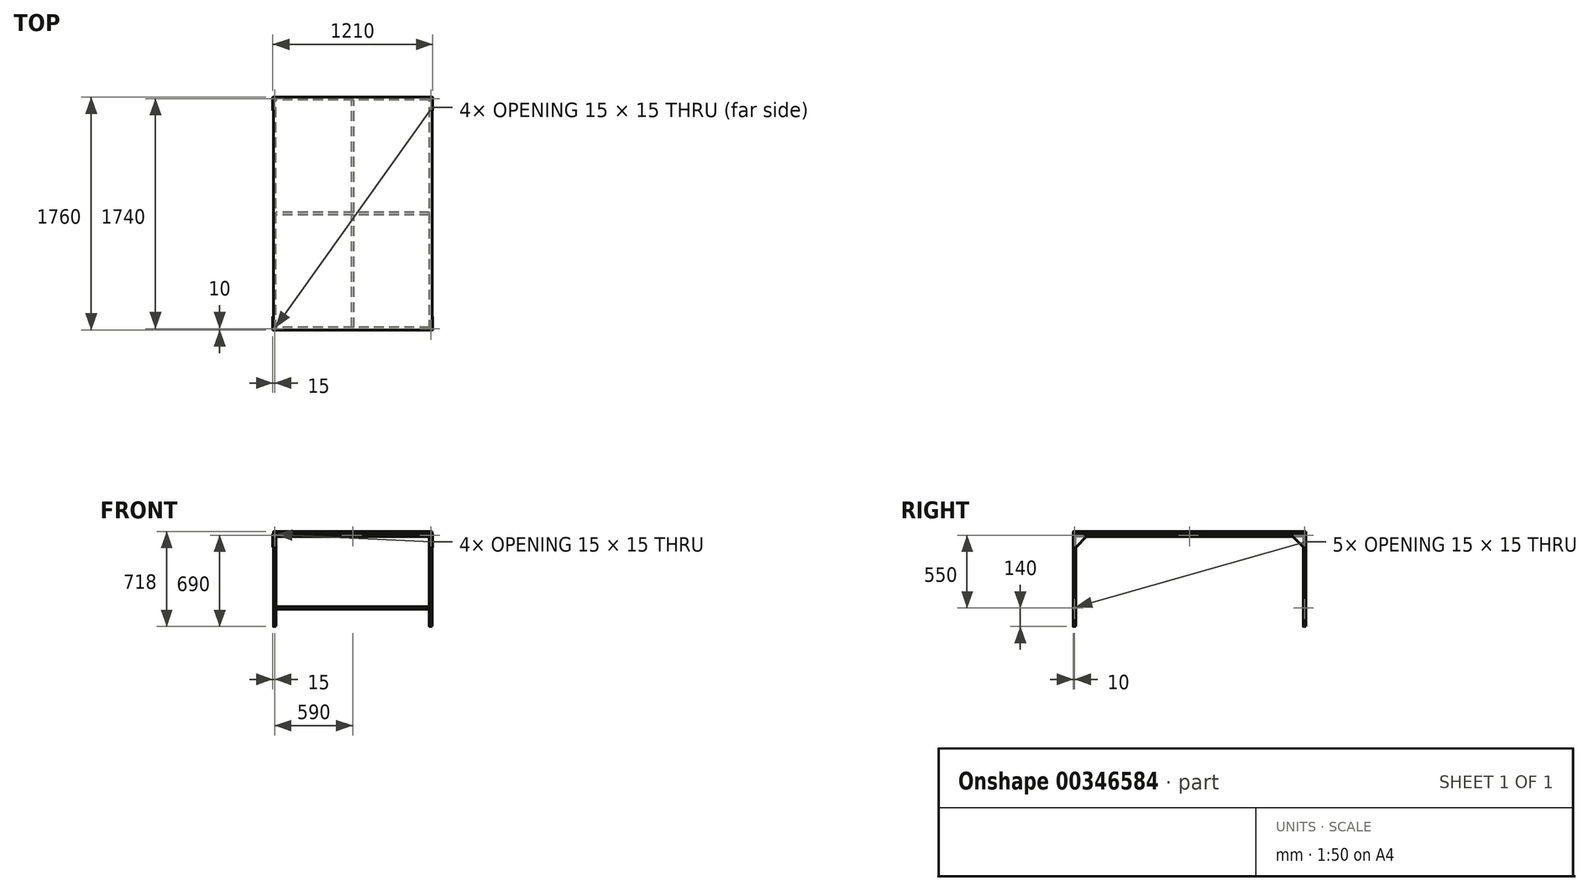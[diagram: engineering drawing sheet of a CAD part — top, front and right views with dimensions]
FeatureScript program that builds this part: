
annotation { "Feature Type Name" : "Feature", "Feature Type Description" : "" }
export const myFeature = defineFeature(function(context is Context, id is Id, definition is map)
    precondition{}
    {
        {
            var Q0;
            Q0=qCreatedBy(makeId("Front.planeOp"),FACE);
            var sketch = newSketch(context, id + "F0", { "sketchPlane" : qUnion([Q0])});
            skLineSegment(sketch, "E0.bottom", {"start": v(585, 20) * mm, "end": v(595, 20) * mm});
            skLineSegment(sketch, "E0.top", {"start": v(585, 0) * mm, "end": v(595, 0) * mm});
            skLineSegment(sketch, "E0.left", {"start": v(580, 15) * mm, "end": v(580, 5) * mm});
            skLineSegment(sketch, "E0.right", {"start": v(600, 15) * mm, "end": v(600, 5) * mm});
            skPoint(sketch, "E1.visualSharp", {"position": v(580, 20) * mm});
            skArc(sketch, "E1.filletArc", {"start": v(585, 20) * mm, "mid": v(581.46, 18.54) * mm, "end": v(580, 15) * mm});
            skPoint(sketch, "E2.visualSharp", {"position": v(600, 20) * mm});
            skArc(sketch, "E2.filletArc", {"start": v(600, 15) * mm, "mid": v(598.54, 18.54) * mm, "end": v(595, 20) * mm});
            skPoint(sketch, "E3.visualSharp", {"position": v(600, 0) * mm});
            skArc(sketch, "E3.filletArc", {"start": v(595, 0) * mm, "mid": v(598.54, 1.46) * mm, "end": v(600, 5) * mm});
            skPoint(sketch, "E4.visualSharp", {"position": v(580, 0) * mm});
            skArc(sketch, "E4.filletArc", {"start": v(580, 5) * mm, "mid": v(581.46, 1.46) * mm, "end": v(585, 0) * mm});
            skArc(sketch, "E5.0", {"start": v(585, 17.5) * mm, "mid": v(583.23, 16.77) * mm, "end": v(582.5, 15) * mm});
            skLineSegment(sketch, "E5.1", {"start": v(582.5, 15) * mm, "end": v(582.5, 5) * mm});
            skLineSegment(sketch, "E5.2", {"start": v(585, 17.5) * mm, "end": v(595, 17.5) * mm});
            skArc(sketch, "E5.3", {"start": v(582.5, 5) * mm, "mid": v(583.23, 3.23) * mm, "end": v(585, 2.5) * mm});
            skArc(sketch, "E5.4", {"start": v(597.5, 15) * mm, "mid": v(596.77, 16.77) * mm, "end": v(595, 17.5) * mm});
            skLineSegment(sketch, "E5.5", {"start": v(597.5, 15) * mm, "end": v(597.5, 5) * mm});
            skArc(sketch, "E5.6", {"start": v(595, 2.5) * mm, "mid": v(596.77, 3.23) * mm, "end": v(597.5, 5) * mm});
            skLineSegment(sketch, "E5.7", {"start": v(585, 2.5) * mm, "end": v(595, 2.5) * mm});
            skSolve(sketch);
        }
        {
            var Q0;
            Q0 = qSketchRegion(id + "F0", true);
            extrude(context, id + "F1", {"entities" : qUnion([Q0]), "endBound" : BoundingType.SYMMETRIC, "depth" : 1760 * mm});
        }
        {
            var Q0;
            Q0=makeQuery(id+"F1.opExtrude","SWEPT_BODY",BODY,{"disambiguationData":[OSD([sQuery(id+"F0.wireOp",EDGE,"E0.bottom"),sQuery(id+"F0.wireOp",EDGE,"E0.top"),sQuery(id+"F0.wireOp",EDGE,"E0.left"),sQuery(id+"F0.wireOp",EDGE,"E0.right"),sQuery(id+"F0.wireOp",EDGE,"E1.filletArc"),sQuery(id+"F0.wireOp",EDGE,"E2.filletArc"),sQuery(id+"F0.wireOp",EDGE,"E3.filletArc"),sQuery(id+"F0.wireOp",EDGE,"E4.filletArc"),sQuery(id+"F0.wireOp",EDGE,"E5.0"),sQuery(id+"F0.wireOp",EDGE,"E5.1"),sQuery(id+"F0.wireOp",EDGE,"E5.2"),sQuery(id+"F0.wireOp",EDGE,"E5.3"),sQuery(id+"F0.wireOp",EDGE,"E5.4"),sQuery(id+"F0.wireOp",EDGE,"E5.5"),sQuery(id+"F0.wireOp",EDGE,"E5.6"),sQuery(id+"F0.wireOp",EDGE,"E5.7")])]});
            transform(context, id + "F2", {"entities" : qUnion([Q0]), "transformType" : TransformType.TRANSLATION_3D, "dx" : -1180 * mm, "dy" : 0 * mm, "dz" : 0 * mm, "makeCopy" : true});
        }
        {
            var Q0;
            Q0=makeQuery(id+"F2.opPattern","COPY",FACE,{"derivedFrom":makeQuery(id+"F1.opExtrude","SWEPT_FACE",FACE,{"disambiguationData":[OSD([sQuery(id+"F0.wireOp",EDGE,"E0.right")])]}),"instanceName":"1"});
            var sketch = newSketch(context, id + "F3", { "sketchPlane" : qUnion([Q0])});
            skLineSegment(sketch, "E6.bottom", {"start": v(-875, 20) * mm, "end": v(-865, 20) * mm});
            skLineSegment(sketch, "E6.top", {"start": v(-875, 0) * mm, "end": v(-865, 0) * mm});
            skLineSegment(sketch, "E6.left", {"start": v(-880, 15) * mm, "end": v(-880, 5) * mm});
            skLineSegment(sketch, "E6.right", {"start": v(-860, 15) * mm, "end": v(-860, 5) * mm});
            skPoint(sketch, "E7.visualSharp", {"position": v(-880, 0) * mm});
            skArc(sketch, "E7.filletArc", {"start": v(-880, 5) * mm, "mid": v(-878.54, 1.46) * mm, "end": v(-875, 0) * mm});
            skPoint(sketch, "E8.visualSharp", {"position": v(-880, 20) * mm});
            skArc(sketch, "E8.filletArc", {"start": v(-875, 20) * mm, "mid": v(-878.54, 18.54) * mm, "end": v(-880, 15) * mm});
            skPoint(sketch, "E9.visualSharp", {"position": v(-860, 20) * mm});
            skArc(sketch, "E9.filletArc", {"start": v(-860, 15) * mm, "mid": v(-861.46, 18.54) * mm, "end": v(-865, 20) * mm});
            skPoint(sketch, "E10.visualSharp", {"position": v(-860, 0) * mm});
            skArc(sketch, "E10.filletArc", {"start": v(-865, 0) * mm, "mid": v(-861.46, 1.46) * mm, "end": v(-860, 5) * mm});
            skLineSegment(sketch, "E11.0", {"start": v(-877.5, 15) * mm, "end": v(-877.5, 5) * mm});
            skArc(sketch, "E11.1", {"start": v(-875, 17.5) * mm, "mid": v(-876.77, 16.77) * mm, "end": v(-877.5, 15) * mm});
            skArc(sketch, "E11.2", {"start": v(-877.5, 5) * mm, "mid": v(-876.77, 3.23) * mm, "end": v(-875, 2.5) * mm});
            skLineSegment(sketch, "E11.3", {"start": v(-875, 17.5) * mm, "end": v(-865, 17.5) * mm});
            skLineSegment(sketch, "E11.4", {"start": v(-875, 2.5) * mm, "end": v(-865, 2.5) * mm});
            skArc(sketch, "E11.5", {"start": v(-865, 2.5) * mm, "mid": v(-863.23, 3.23) * mm, "end": v(-862.5, 5) * mm});
            skLineSegment(sketch, "E11.6", {"start": v(-862.5, 15) * mm, "end": v(-862.5, 5) * mm});
            skArc(sketch, "E11.7", {"start": v(-862.5, 15) * mm, "mid": v(-863.23, 16.77) * mm, "end": v(-865, 17.5) * mm});
            skSolve(sketch);
        }
        {
            var Q0;
            Q0 = qSketchRegion(id + "F3", true);
            extrude(context, id + "F4", {"entities" : qUnion([Q0]), "depth" : 1160 * mm});
        }
        {
            var Q0;
            Q0=makeQuery(id+"F4.opExtrude","SWEPT_BODY",BODY,{"disambiguationData":[OSD([sQuery(id+"F3.wireOp",EDGE,"E6.bottom"),sQuery(id+"F3.wireOp",EDGE,"E6.top"),sQuery(id+"F3.wireOp",EDGE,"E6.left"),sQuery(id+"F3.wireOp",EDGE,"E6.right"),sQuery(id+"F3.wireOp",EDGE,"E7.filletArc"),sQuery(id+"F3.wireOp",EDGE,"E8.filletArc"),sQuery(id+"F3.wireOp",EDGE,"E9.filletArc"),sQuery(id+"F3.wireOp",EDGE,"E10.filletArc"),sQuery(id+"F3.wireOp",EDGE,"E11.0"),sQuery(id+"F3.wireOp",EDGE,"E11.1"),sQuery(id+"F3.wireOp",EDGE,"E11.2"),sQuery(id+"F3.wireOp",EDGE,"E11.3"),sQuery(id+"F3.wireOp",EDGE,"E11.4"),sQuery(id+"F3.wireOp",EDGE,"E11.5"),sQuery(id+"F3.wireOp",EDGE,"E11.6"),sQuery(id+"F3.wireOp",EDGE,"E11.7")])]});
            transform(context, id + "F5", {"entities" : qUnion([Q0]), "transformType" : TransformType.TRANSLATION_3D, "dx" : 0 * mm, "dy" : 1740 * mm, "dz" : 0 * mm, "makeCopy" : true});
        }
        {
            var Q0;
            Q0=makeQuery(id+"F4.opExtrude","SWEPT_BODY",BODY,{"disambiguationData":[OSD([sQuery(id+"F3.wireOp",EDGE,"E6.bottom"),sQuery(id+"F3.wireOp",EDGE,"E6.top"),sQuery(id+"F3.wireOp",EDGE,"E6.left"),sQuery(id+"F3.wireOp",EDGE,"E6.right"),sQuery(id+"F3.wireOp",EDGE,"E7.filletArc"),sQuery(id+"F3.wireOp",EDGE,"E8.filletArc"),sQuery(id+"F3.wireOp",EDGE,"E9.filletArc"),sQuery(id+"F3.wireOp",EDGE,"E10.filletArc"),sQuery(id+"F3.wireOp",EDGE,"E11.0"),sQuery(id+"F3.wireOp",EDGE,"E11.1"),sQuery(id+"F3.wireOp",EDGE,"E11.2"),sQuery(id+"F3.wireOp",EDGE,"E11.3"),sQuery(id+"F3.wireOp",EDGE,"E11.4"),sQuery(id+"F3.wireOp",EDGE,"E11.5"),sQuery(id+"F3.wireOp",EDGE,"E11.6"),sQuery(id+"F3.wireOp",EDGE,"E11.7")])]});
            transform(context, id + "F6", {"entities" : qUnion([Q0]), "transformType" : TransformType.TRANSLATION_3D, "dx" : 0 * mm, "dy" : 870 * mm, "dz" : 0 * mm, "makeCopy" : true});
        }
        {
            var Q0;
            Q0=makeQuery(id+"F1.opExtrude","SWEPT_FACE",FACE,{"disambiguationData":[OSD([sQuery(id+"F0.wireOp",EDGE,"E0.top")])]});
            var sketch = newSketch(context, id + "F7", { "sketchPlane" : qUnion([Q0])});
            skLineSegment(sketch, "E12.bottom", {"start": v(595, -880) * mm, "end": v(585, -880) * mm});
            skLineSegment(sketch, "E12.top", {"start": v(595, -860) * mm, "end": v(585, -860) * mm});
            skLineSegment(sketch, "E12.left", {"start": v(600, -875) * mm, "end": v(600, -865) * mm});
            skLineSegment(sketch, "E12.right", {"start": v(580, -875) * mm, "end": v(580, -865) * mm});
            skPoint(sketch, "E13.visualSharp", {"position": v(600, -860) * mm});
            skArc(sketch, "E13.filletArc", {"start": v(600, -865) * mm, "mid": v(598.54, -861.46) * mm, "end": v(595, -860) * mm});
            skPoint(sketch, "E14.visualSharp", {"position": v(580, -860) * mm});
            skArc(sketch, "E14.filletArc", {"start": v(585, -860) * mm, "mid": v(581.46, -861.46) * mm, "end": v(580, -865) * mm});
            skPoint(sketch, "E15.visualSharp", {"position": v(580, -880) * mm});
            skArc(sketch, "E15.filletArc", {"start": v(580, -875) * mm, "mid": v(581.46, -878.54) * mm, "end": v(585, -880) * mm});
            skPoint(sketch, "E16.visualSharp", {"position": v(600, -880) * mm});
            skArc(sketch, "E16.filletArc", {"start": v(595, -880) * mm, "mid": v(598.54, -878.54) * mm, "end": v(600, -875) * mm});
            skArc(sketch, "E17.0", {"start": v(582.5, -875) * mm, "mid": v(583.23, -876.77) * mm, "end": v(585, -877.5) * mm});
            skLineSegment(sketch, "E17.1", {"start": v(595, -877.5) * mm, "end": v(585, -877.5) * mm});
            skLineSegment(sketch, "E17.2", {"start": v(582.5, -875) * mm, "end": v(582.5, -865) * mm});
            skArc(sketch, "E17.3", {"start": v(595, -877.5) * mm, "mid": v(596.77, -876.77) * mm, "end": v(597.5, -875) * mm});
            skArc(sketch, "E17.4", {"start": v(585, -862.5) * mm, "mid": v(583.23, -863.23) * mm, "end": v(582.5, -865) * mm});
            skLineSegment(sketch, "E17.5", {"start": v(595, -862.5) * mm, "end": v(585, -862.5) * mm});
            skArc(sketch, "E17.6", {"start": v(597.5, -865) * mm, "mid": v(596.77, -863.23) * mm, "end": v(595, -862.5) * mm});
            skLineSegment(sketch, "E17.7", {"start": v(597.5, -875) * mm, "end": v(597.5, -865) * mm});
            skSolve(sketch);
        }
        {
            var Q0;
            Q0 = qSketchRegion(id + "F7", true);
            extrude(context, id + "F8", {"entities" : qUnion([Q0]), "depth" : 680 * mm});
        }
        {
            var Q0;
            Q0=makeQuery(id+"F8.opExtrude","SWEPT_BODY",BODY,{"disambiguationData":[OSD([sQuery(id+"F7.wireOp",EDGE,"E12.bottom"),sQuery(id+"F7.wireOp",EDGE,"E12.top"),sQuery(id+"F7.wireOp",EDGE,"E12.left"),sQuery(id+"F7.wireOp",EDGE,"E12.right"),sQuery(id+"F7.wireOp",EDGE,"E13.filletArc"),sQuery(id+"F7.wireOp",EDGE,"E14.filletArc"),sQuery(id+"F7.wireOp",EDGE,"E15.filletArc"),sQuery(id+"F7.wireOp",EDGE,"E16.filletArc"),sQuery(id+"F7.wireOp",EDGE,"E17.0"),sQuery(id+"F7.wireOp",EDGE,"E17.1"),sQuery(id+"F7.wireOp",EDGE,"E17.2"),sQuery(id+"F7.wireOp",EDGE,"E17.3"),sQuery(id+"F7.wireOp",EDGE,"E17.4"),sQuery(id+"F7.wireOp",EDGE,"E17.5"),sQuery(id+"F7.wireOp",EDGE,"E17.6"),sQuery(id+"F7.wireOp",EDGE,"E17.7")])]});
            transform(context, id + "F9", {"entities" : qUnion([Q0]), "transformType" : TransformType.TRANSLATION_3D, "dx" : -1180 * mm, "dy" : 0 * mm, "dz" : 0 * mm, "makeCopy" : true});
        }
        {
            var Q0;
            Q0=makeQuery(id+"F9.opPattern","COPY",BODY,{"derivedFrom":makeQuery(id+"F8.opExtrude","SWEPT_BODY",BODY,{"disambiguationData":[OSD([sQuery(id+"F7.wireOp",EDGE,"E12.bottom"),sQuery(id+"F7.wireOp",EDGE,"E12.top"),sQuery(id+"F7.wireOp",EDGE,"E12.left"),sQuery(id+"F7.wireOp",EDGE,"E12.right"),sQuery(id+"F7.wireOp",EDGE,"E13.filletArc"),sQuery(id+"F7.wireOp",EDGE,"E14.filletArc"),sQuery(id+"F7.wireOp",EDGE,"E15.filletArc"),sQuery(id+"F7.wireOp",EDGE,"E16.filletArc"),sQuery(id+"F7.wireOp",EDGE,"E17.0"),sQuery(id+"F7.wireOp",EDGE,"E17.1"),sQuery(id+"F7.wireOp",EDGE,"E17.2"),sQuery(id+"F7.wireOp",EDGE,"E17.3"),sQuery(id+"F7.wireOp",EDGE,"E17.4"),sQuery(id+"F7.wireOp",EDGE,"E17.5"),sQuery(id+"F7.wireOp",EDGE,"E17.6"),sQuery(id+"F7.wireOp",EDGE,"E17.7")])]}),"instanceName":"1"});
            var Q1;
            Q1=makeQuery(id+"F8.opExtrude","SWEPT_BODY",BODY,{"disambiguationData":[OSD([sQuery(id+"F7.wireOp",EDGE,"E12.bottom"),sQuery(id+"F7.wireOp",EDGE,"E12.top"),sQuery(id+"F7.wireOp",EDGE,"E12.left"),sQuery(id+"F7.wireOp",EDGE,"E12.right"),sQuery(id+"F7.wireOp",EDGE,"E13.filletArc"),sQuery(id+"F7.wireOp",EDGE,"E14.filletArc"),sQuery(id+"F7.wireOp",EDGE,"E15.filletArc"),sQuery(id+"F7.wireOp",EDGE,"E16.filletArc"),sQuery(id+"F7.wireOp",EDGE,"E17.0"),sQuery(id+"F7.wireOp",EDGE,"E17.1"),sQuery(id+"F7.wireOp",EDGE,"E17.2"),sQuery(id+"F7.wireOp",EDGE,"E17.3"),sQuery(id+"F7.wireOp",EDGE,"E17.4"),sQuery(id+"F7.wireOp",EDGE,"E17.5"),sQuery(id+"F7.wireOp",EDGE,"E17.6"),sQuery(id+"F7.wireOp",EDGE,"E17.7")])]});
            transform(context, id + "F10", {"entities" : qUnion([Q0, Q1]), "transformType" : TransformType.TRANSLATION_3D, "dx" : 0 * mm, "dy" : -1740 * mm, "dz" : 0 * mm, "makeCopy" : true});
        }
        {
            var Q0;
            Q0=makeQuery(id+"F5.opPattern","COPY",BODY,{"derivedFrom":makeQuery(id+"F4.opExtrude","SWEPT_BODY",BODY,{"disambiguationData":[OSD([sQuery(id+"F3.wireOp",EDGE,"E6.bottom"),sQuery(id+"F3.wireOp",EDGE,"E6.top"),sQuery(id+"F3.wireOp",EDGE,"E6.left"),sQuery(id+"F3.wireOp",EDGE,"E6.right"),sQuery(id+"F3.wireOp",EDGE,"E7.filletArc"),sQuery(id+"F3.wireOp",EDGE,"E8.filletArc"),sQuery(id+"F3.wireOp",EDGE,"E9.filletArc"),sQuery(id+"F3.wireOp",EDGE,"E10.filletArc"),sQuery(id+"F3.wireOp",EDGE,"E11.0"),sQuery(id+"F3.wireOp",EDGE,"E11.1"),sQuery(id+"F3.wireOp",EDGE,"E11.2"),sQuery(id+"F3.wireOp",EDGE,"E11.3"),sQuery(id+"F3.wireOp",EDGE,"E11.4"),sQuery(id+"F3.wireOp",EDGE,"E11.5"),sQuery(id+"F3.wireOp",EDGE,"E11.6"),sQuery(id+"F3.wireOp",EDGE,"E11.7")])]}),"instanceName":"1"});
            var Q1;
            Q1=makeQuery(id+"F4.opExtrude","SWEPT_BODY",BODY,{"disambiguationData":[OSD([sQuery(id+"F3.wireOp",EDGE,"E6.bottom"),sQuery(id+"F3.wireOp",EDGE,"E6.top"),sQuery(id+"F3.wireOp",EDGE,"E6.left"),sQuery(id+"F3.wireOp",EDGE,"E6.right"),sQuery(id+"F3.wireOp",EDGE,"E7.filletArc"),sQuery(id+"F3.wireOp",EDGE,"E8.filletArc"),sQuery(id+"F3.wireOp",EDGE,"E9.filletArc"),sQuery(id+"F3.wireOp",EDGE,"E10.filletArc"),sQuery(id+"F3.wireOp",EDGE,"E11.0"),sQuery(id+"F3.wireOp",EDGE,"E11.1"),sQuery(id+"F3.wireOp",EDGE,"E11.2"),sQuery(id+"F3.wireOp",EDGE,"E11.3"),sQuery(id+"F3.wireOp",EDGE,"E11.4"),sQuery(id+"F3.wireOp",EDGE,"E11.5"),sQuery(id+"F3.wireOp",EDGE,"E11.6"),sQuery(id+"F3.wireOp",EDGE,"E11.7")])]});
            transform(context, id + "F11", {"entities" : qUnion([Q0, Q1]), "transformType" : TransformType.TRANSLATION_3D, "dx" : 0 * mm, "dy" : 0 * mm, "dz" : -550 * mm, "makeCopy" : true});
        }
        {
            var Q0;
            Q0=makeQuery(id+"F1.opExtrude","SWEPT_FACE",FACE,{"disambiguationData":[OSD([sQuery(id+"F0.wireOp",EDGE,"E0.right")])]});
            var sketch = newSketch(context, id + "F12", { "sketchPlane" : qUnion([Q0])});
            skLineSegment(sketch, "E18", {"start": v(-880, 20) * mm, "end": v(-780, 20) * mm});
            skLineSegment(sketch, "E19", {"start": v(-780, 20) * mm, "end": v(-780, 0) * mm});
            skLineSegment(sketch, "E20", {"start": v(-780, 0) * mm, "end": v(-860, -80) * mm});
            skLineSegment(sketch, "E21", {"start": v(-860, -80) * mm, "end": v(-880, -80) * mm});
            skLineSegment(sketch, "E22", {"start": v(-880, -80) * mm, "end": v(-880, 20) * mm});
            skSolve(sketch);
        }
        {
            var Q0;
            Q0 = qSketchRegion(id + "F12", true);
            extrude(context, id + "F13", {"entities" : qUnion([Q0]), "depth" : 5 * mm});
        }
        {
            var Q0;
            Q0=makeQuery(id+"F13.opExtrude","SWEPT_EDGE",EDGE,{"disambiguationData":[OSD([sQuery(id+"F12.wireOp",EDGE,"E18"),sQuery(id+"F12.wireOp",EDGE,"E22")])]});
            var Q1;
            Q1=makeQuery(id+"F13.opExtrude","SWEPT_EDGE",EDGE,{"disambiguationData":[OSD([sQuery(id+"F12.wireOp",EDGE,"E21"),sQuery(id+"F12.wireOp",EDGE,"E22")])]});
            var Q2;
            Q2=makeQuery(id+"F13.opExtrude","SWEPT_EDGE",EDGE,{"disambiguationData":[OSD([sQuery(id+"F12.wireOp",EDGE,"E18"),sQuery(id+"F12.wireOp",EDGE,"E19")])]});
            var Q3;
            Q3=makeQuery(id+"F13.opExtrude","SWEPT_EDGE",EDGE,{"disambiguationData":[OSD([sQuery(id+"F12.wireOp",EDGE,"E19"),sQuery(id+"F12.wireOp",EDGE,"E20")])]});
            var Q4;
            Q4=makeQuery(id+"F13.opExtrude","SWEPT_EDGE",EDGE,{"disambiguationData":[OSD([sQuery(id+"F12.wireOp",EDGE,"E20"),sQuery(id+"F12.wireOp",EDGE,"E21")])]});
            fillet(context, id + "F14", {"entities" : qUnion([Q0, Q1, Q2, Q3, Q4]), "radius" : 5 * mm, "tangentPropagation" : true, "allowEdgeOverflow" : false});
        }
        {
            var Q0;
            Q0=makeQuery(id+"F13.opExtrude","SWEPT_BODY",BODY,{"disambiguationData":[OSD([sQuery(id+"F12.wireOp",EDGE,"E18"),sQuery(id+"F12.wireOp",EDGE,"E19"),sQuery(id+"F12.wireOp",EDGE,"E20"),sQuery(id+"F12.wireOp",EDGE,"E21"),sQuery(id+"F12.wireOp",EDGE,"E22")])]});
            transform(context, id + "F15", {"entities" : qUnion([Q0]), "transformType" : TransformType.TRANSLATION_3D, "dx" : -1205 * mm, "dy" : 0 * mm, "dz" : 0 * mm, "makeCopy" : true});
        }
        {
            var Q0;
            Q0=makeQuery(id+"F1.opExtrude","SWEPT_FACE",FACE,{"disambiguationData":[OSD([sQuery(id+"F0.wireOp",EDGE,"E0.right")])]});
            var sketch = newSketch(context, id + "F16", { "sketchPlane" : qUnion([Q0])});
            skLineSegment(sketch, "E23", {"start": v(880, 20) * mm, "end": v(780, 20) * mm});
            skLineSegment(sketch, "E24", {"start": v(780, 20) * mm, "end": v(780, 0) * mm});
            skLineSegment(sketch, "E25", {"start": v(780, 0) * mm, "end": v(860, -80) * mm});
            skLineSegment(sketch, "E26", {"start": v(860, -80) * mm, "end": v(880, -80) * mm});
            skLineSegment(sketch, "E27", {"start": v(880, -80) * mm, "end": v(880, 20) * mm});
            skSolve(sketch);
        }
        {
            var Q0;
            Q0 = qSketchRegion(id + "F16", true);
            extrude(context, id + "F17", {"entities" : qUnion([Q0]), "depth" : 5 * mm});
        }
        {
            var Q0;
            Q0=makeQuery(id+"F17.opExtrude","SWEPT_EDGE",EDGE,{"disambiguationData":[OSD([sQuery(id+"F16.wireOp",EDGE,"E23"),sQuery(id+"F16.wireOp",EDGE,"E27")])]});
            var Q1;
            Q1=makeQuery(id+"F17.opExtrude","SWEPT_EDGE",EDGE,{"disambiguationData":[OSD([sQuery(id+"F16.wireOp",EDGE,"E26"),sQuery(id+"F16.wireOp",EDGE,"E27")])]});
            var Q2;
            Q2=makeQuery(id+"F17.opExtrude","SWEPT_EDGE",EDGE,{"disambiguationData":[OSD([sQuery(id+"F16.wireOp",EDGE,"E23"),sQuery(id+"F16.wireOp",EDGE,"E24")])]});
            var Q3;
            Q3=makeQuery(id+"F17.opExtrude","SWEPT_EDGE",EDGE,{"disambiguationData":[OSD([sQuery(id+"F16.wireOp",EDGE,"E24"),sQuery(id+"F16.wireOp",EDGE,"E25")])]});
            var Q4;
            Q4=makeQuery(id+"F17.opExtrude","SWEPT_EDGE",EDGE,{"disambiguationData":[OSD([sQuery(id+"F16.wireOp",EDGE,"E25"),sQuery(id+"F16.wireOp",EDGE,"E26")])]});
            fillet(context, id + "F18", {"entities" : qUnion([Q0, Q1, Q2, Q3, Q4]), "radius" : 5 * mm, "tangentPropagation" : true, "allowEdgeOverflow" : false});
        }
        {
            var Q0;
            Q0=makeQuery(id+"F17.opExtrude","SWEPT_BODY",BODY,{"disambiguationData":[OSD([sQuery(id+"F16.wireOp",EDGE,"E23"),sQuery(id+"F16.wireOp",EDGE,"E24"),sQuery(id+"F16.wireOp",EDGE,"E25"),sQuery(id+"F16.wireOp",EDGE,"E26"),sQuery(id+"F16.wireOp",EDGE,"E27")])]});
            transform(context, id + "F19", {"entities" : qUnion([Q0]), "transformType" : TransformType.TRANSLATION_3D, "dx" : -1205 * mm, "dy" : 0 * mm, "dz" : 0 * mm, "makeCopy" : true});
        }
        {
            var Q0;
            Q0=makeQuery(id+"F5.opPattern","COPY",FACE,{"derivedFrom":makeQuery(id+"F4.opExtrude","SWEPT_FACE",FACE,{"disambiguationData":[OSD([sQuery(id+"F3.wireOp",EDGE,"E6.left")])]}),"instanceName":"1"});
            var sketch = newSketch(context, id + "F20", { "sketchPlane" : qUnion([Q0])});
            skLineSegment(sketch, "E28.bottom", {"start": v(-5, 20) * mm, "end": v(5, 20) * mm});
            skLineSegment(sketch, "E28.top", {"start": v(-5, 0) * mm, "end": v(5, 0) * mm});
            skLineSegment(sketch, "E28.left", {"start": v(-10, 15) * mm, "end": v(-10, 5) * mm});
            skLineSegment(sketch, "E28.right", {"start": v(10, 15) * mm, "end": v(10, 5) * mm});
            skPoint(sketch, "E29.visualSharp", {"position": v(-10, 20) * mm});
            skArc(sketch, "E29.filletArc", {"start": v(-5, 20) * mm, "mid": v(-8.54, 18.54) * mm, "end": v(-10, 15) * mm});
            skPoint(sketch, "E30.visualSharp", {"position": v(-10, 0) * mm});
            skArc(sketch, "E30.filletArc", {"start": v(-10, 5) * mm, "mid": v(-8.54, 1.46) * mm, "end": v(-5, 0) * mm});
            skPoint(sketch, "E31.visualSharp", {"position": v(10, 0) * mm});
            skArc(sketch, "E31.filletArc", {"start": v(5, 0) * mm, "mid": v(8.54, 1.46) * mm, "end": v(10, 5) * mm});
            skPoint(sketch, "E32.visualSharp", {"position": v(10, 20) * mm});
            skArc(sketch, "E32.filletArc", {"start": v(10, 15) * mm, "mid": v(8.54, 18.54) * mm, "end": v(5, 20) * mm});
            skLineSegment(sketch, "E33.0", {"start": v(-5, 17.5) * mm, "end": v(5, 17.5) * mm});
            skArc(sketch, "E33.1", {"start": v(7.5, 15) * mm, "mid": v(6.77, 16.77) * mm, "end": v(5, 17.5) * mm});
            skArc(sketch, "E33.2", {"start": v(-5, 17.5) * mm, "mid": v(-6.77, 16.77) * mm, "end": v(-7.5, 15) * mm});
            skLineSegment(sketch, "E33.3", {"start": v(7.5, 15) * mm, "end": v(7.5, 5) * mm});
            skLineSegment(sketch, "E33.4", {"start": v(-7.5, 15) * mm, "end": v(-7.5, 5) * mm});
            skArc(sketch, "E33.5", {"start": v(-7.5, 5) * mm, "mid": v(-6.77, 3.23) * mm, "end": v(-5, 2.5) * mm});
            skLineSegment(sketch, "E33.6", {"start": v(-5, 2.5) * mm, "end": v(5, 2.5) * mm});
            skArc(sketch, "E33.7", {"start": v(5, 2.5) * mm, "mid": v(6.77, 3.23) * mm, "end": v(7.5, 5) * mm});
            skSolve(sketch);
        }
        {
            var Q0;
            Q0 = qSketchRegion(id + "F20", true);
            extrude(context, id + "F21", {"entities" : qUnion([Q0]), "depth" : 850 * mm});
        }
        {
            var Q0;
            Q0=makeQuery(id+"F21.opExtrude","SWEPT_BODY",BODY,{"disambiguationData":[OSD([sQuery(id+"F20.wireOp",EDGE,"E28.bottom"),sQuery(id+"F20.wireOp",EDGE,"E28.top"),sQuery(id+"F20.wireOp",EDGE,"E28.left"),sQuery(id+"F20.wireOp",EDGE,"E28.right"),sQuery(id+"F20.wireOp",EDGE,"E29.filletArc"),sQuery(id+"F20.wireOp",EDGE,"E30.filletArc"),sQuery(id+"F20.wireOp",EDGE,"E31.filletArc"),sQuery(id+"F20.wireOp",EDGE,"E32.filletArc"),sQuery(id+"F20.wireOp",EDGE,"E33.0"),sQuery(id+"F20.wireOp",EDGE,"E33.1"),sQuery(id+"F20.wireOp",EDGE,"E33.2"),sQuery(id+"F20.wireOp",EDGE,"E33.3"),sQuery(id+"F20.wireOp",EDGE,"E33.4"),sQuery(id+"F20.wireOp",EDGE,"E33.5"),sQuery(id+"F20.wireOp",EDGE,"E33.6"),sQuery(id+"F20.wireOp",EDGE,"E33.7")])]});
            transform(context, id + "F22", {"entities" : qUnion([Q0]), "transformType" : TransformType.TRANSLATION_3D, "dx" : 0 * mm, "dy" : -870 * mm, "dz" : 0 * mm, "makeCopy" : true});
        }
        {
            var Q0;
            Q0=makeQuery(id+"F4.opExtrude","SWEPT_FACE",FACE,{"disambiguationData":[OSD([sQuery(id+"F3.wireOp",EDGE,"E6.bottom")])]});
            var sketch = newSketch(context, id + "F23", { "sketchPlane" : qUnion([Q0])});
            skLineSegment(sketch, "E34.bottom", {"start": v(-600, -880) * mm, "end": v(600, -880) * mm});
            skLineSegment(sketch, "E34.top", {"start": v(-600, 880) * mm, "end": v(600, 880) * mm});
            skLineSegment(sketch, "E34.left", {"start": v(-600, -880) * mm, "end": v(-600, 880) * mm});
            skLineSegment(sketch, "E34.right", {"start": v(600, -880) * mm, "end": v(600, 880) * mm});
            skSolve(sketch);
        }
        {
            var Q0;
            Q0 = qSketchRegion(id + "F23", true);
            extrude(context, id + "F24", {"entities" : qUnion([Q0]), "depth" : 18 * mm});
        }
        {
            var Q0;
            Q0=makeQuery(id+"F24.opExtrude","SWEPT_EDGE",EDGE,{"disambiguationData":[OSD([sQuery(id+"F23.wireOp",EDGE,"E34.top"),sQuery(id+"F23.wireOp",EDGE,"E34.right")])]});
            var Q1;
            Q1=makeQuery(id+"F24.opExtrude","SWEPT_EDGE",EDGE,{"disambiguationData":[OSD([sQuery(id+"F23.wireOp",EDGE,"E34.bottom"),sQuery(id+"F23.wireOp",EDGE,"E34.right")])]});
            var Q2;
            Q2=makeQuery(id+"F24.opExtrude","SWEPT_EDGE",EDGE,{"disambiguationData":[OSD([sQuery(id+"F23.wireOp",EDGE,"E34.top"),sQuery(id+"F23.wireOp",EDGE,"E34.left")])]});
            var Q3;
            Q3=makeQuery(id+"F24.opExtrude","SWEPT_EDGE",EDGE,{"disambiguationData":[OSD([sQuery(id+"F23.wireOp",EDGE,"E34.bottom"),sQuery(id+"F23.wireOp",EDGE,"E34.left")])]});
            fillet(context, id + "F25", {"entities" : qUnion([Q0, Q1, Q2, Q3]), "radius" : 5 * mm, "tangentPropagation" : true, "allowEdgeOverflow" : false});
        }
    });
